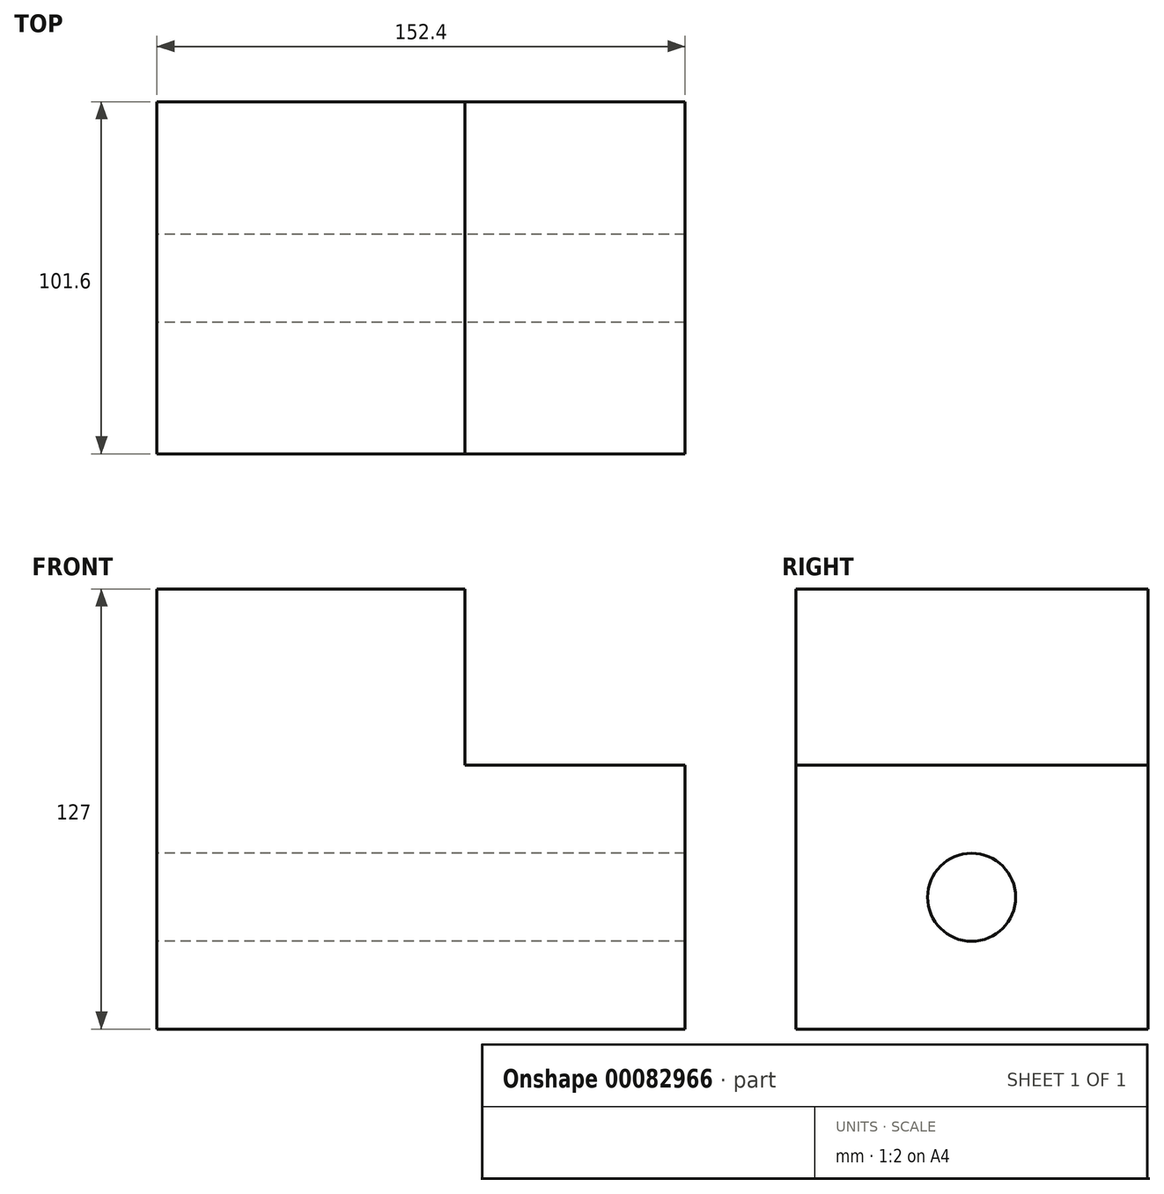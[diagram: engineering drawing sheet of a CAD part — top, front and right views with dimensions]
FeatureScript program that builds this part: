
annotation { "Feature Type Name" : "Feature", "Feature Type Description" : "" }
export const myFeature = defineFeature(function(context is Context, id is Id, definition is map)
    precondition{}
    {
        {
            var Q0;
            Q0=qCreatedBy(makeId("Front.planeOp"),FACE);
            var sketch = newSketch(context, id + "F0", { "sketchPlane" : qUnion([Q0])});
            skLineSegment(sketch, "E0", {"start": v(0, 0) * mm, "end": v(152.4, 0) * mm});
            skLineSegment(sketch, "E1", {"start": v(152.4, 0) * mm, "end": v(152.4, 127) * mm});
            skLineSegment(sketch, "E2", {"start": v(152.4, 127) * mm, "end": v(0, 127) * mm});
            skLineSegment(sketch, "E3", {"start": v(0, 127) * mm, "end": v(0, 0) * mm});
            skSolve(sketch);
        }
        {
            var Q0;
            Q0=makeQuery(id+"F0.imprint","IMPRINT",FACE,{"disambiguationData":[TD([[makeQuery(id+"F0.imprint","IMPRINT",EDGE,{"derivedFrom":sQuery(id+"F0.wireOp",EDGE,"E0")}),1.0]])]});
            extrude(context, id + "F1", {"entities" : qUnion([Q0]), "depth" : 101.6 * mm});
        }
        {
            var Q0;
            Q0 = qSketchRegion(id + "F0", true);
            extrude(context, id + "F2", {"entities" : qUnion([Q0]), "operationType" : NewBodyOperationType.ADD, "depth" : 101.6 * mm});
        }
        {
            var Q0;
            Q0=makeQuery(id+"F1.opExtrude","CAP_FACE",FACE,{"disambiguationData":[OSD([sQuery(id+"F0.wireOp",EDGE,"E0"),sQuery(id+"F0.wireOp",EDGE,"E1"),sQuery(id+"F0.wireOp",EDGE,"E2"),sQuery(id+"F0.wireOp",EDGE,"E3")])],"isStart":false});
            var sketch = newSketch(context, id + "F3", { "sketchPlane" : qUnion([Q0])});
            skLineSegment(sketch, "E4.bottom", {"start": v(152.4, 127) * mm, "end": v(88.9, 127) * mm});
            skLineSegment(sketch, "E4.top", {"start": v(152.4, 76.2) * mm, "end": v(88.9, 76.2) * mm});
            skLineSegment(sketch, "E4.left", {"start": v(152.4, 127) * mm, "end": v(152.4, 76.2) * mm});
            skLineSegment(sketch, "E4.right", {"start": v(88.9, 127) * mm, "end": v(88.9, 76.2) * mm});
            skSolve(sketch);
        }
        {
            var Q0;
            Q0=makeQuery(id+"F3.imprint","IMPRINT",FACE,{"disambiguationData":[TD([[makeQuery(id+"F3.imprint","IMPRINT",EDGE,{"derivedFrom":sQuery(id+"F3.wireOp",EDGE,"E4.bottom")}),1.0]])]});
            extrude(context, id + "F4", {"entities" : qUnion([Q0]), "operationType" : NewBodyOperationType.REMOVE, "endBound" : BoundingType.THROUGH_ALL, "oppositeDirection" : true, "depth" : 25.4 * mm});
        }
        {
            var Q0;
            Q0=makeQuery(id+"F1.opExtrude","SWEPT_FACE",FACE,{"disambiguationData":[OSD([sQuery(id+"F0.wireOp",EDGE,"E3")])]});
            var sketch = newSketch(context, id + "F5", { "sketchPlane" : qUnion([Q0])});
            skLineSegment(sketch, "E5.bottom", {"start": v(0, 0) * mm, "end": v(50.8, 0) * mm});
            skLineSegment(sketch, "E5.top", {"start": v(0, 38.1) * mm, "end": v(50.8, 38.1) * mm});
            skLineSegment(sketch, "E5.left", {"start": v(0, 0) * mm, "end": v(0, 38.1) * mm});
            skLineSegment(sketch, "E5.right", {"start": v(50.8, 0) * mm, "end": v(50.8, 38.1) * mm});
            skSolve(sketch);
        }
        {
            var Q0;
            {var subQ5=sQuery(id+"F5.wireOp",EDGE,"E5.top");Q0=makeQuery(id+"F5.imprint","IMPRINT",FACE,{"disambiguationData":[TD([[makeQuery(id+"F5.imprint","IMPRINT",EDGE,{"derivedFrom":subQ5}),1.0]])]});}
            var sketch = newSketch(context, id + "F6", { "sketchPlane" : qUnion([Q0])});
            skCircle(sketch, "E6", {"center": v(50.93, 38.03) * mm, "radius": 12.7 * mm});
            skSolve(sketch);
        }
        {
            var Q0;
            {var subQ0=sQuery(id+"F6.wireOp",EDGE,"E6");var subQ1=makeQuery(id+"F5.imprint","IMPRINT",EDGE,{"derivedFrom":sQuery(id+"F5.wireOp",EDGE,"E5.top")});var subQ2=makeQuery(id+"F6.imprint","INTERSECT",VERTEX,{"derivedFrom":[subQ1,subQ0]});Q0=makeQuery(id+"F6.imprint","IMPRINT",FACE,{"disambiguationData":[TD([[makeQuery(id+"F6.imprint","IMPRINT",EDGE,{"disambiguationData":[TD([[subQ2,-1.0]])],"derivedFrom":subQ0}),1.0]])]});}
            var Q1;
            {var subQ0=sQuery(id+"F6.wireOp",EDGE,"E6");var subQ1=makeQuery(id+"F5.imprint","IMPRINT",EDGE,{"derivedFrom":sQuery(id+"F5.wireOp",EDGE,"E5.top")});var subQ2=makeQuery(id+"F6.imprint","INTERSECT",VERTEX,{"derivedFrom":[subQ1,subQ0]});Q1=makeQuery(id+"F6.imprint","IMPRINT",FACE,{"disambiguationData":[TD([[makeQuery(id+"F6.imprint","IMPRINT",EDGE,{"disambiguationData":[TD([[subQ2,1.0]])],"derivedFrom":subQ0}),1.0]])]});}
            extrude(context, id + "F7", {"entities" : qUnion([Q0, Q1]), "operationType" : NewBodyOperationType.REMOVE, "endBound" : BoundingType.THROUGH_ALL, "oppositeDirection" : true, "depth" : 25.4 * mm});
        }
    });
